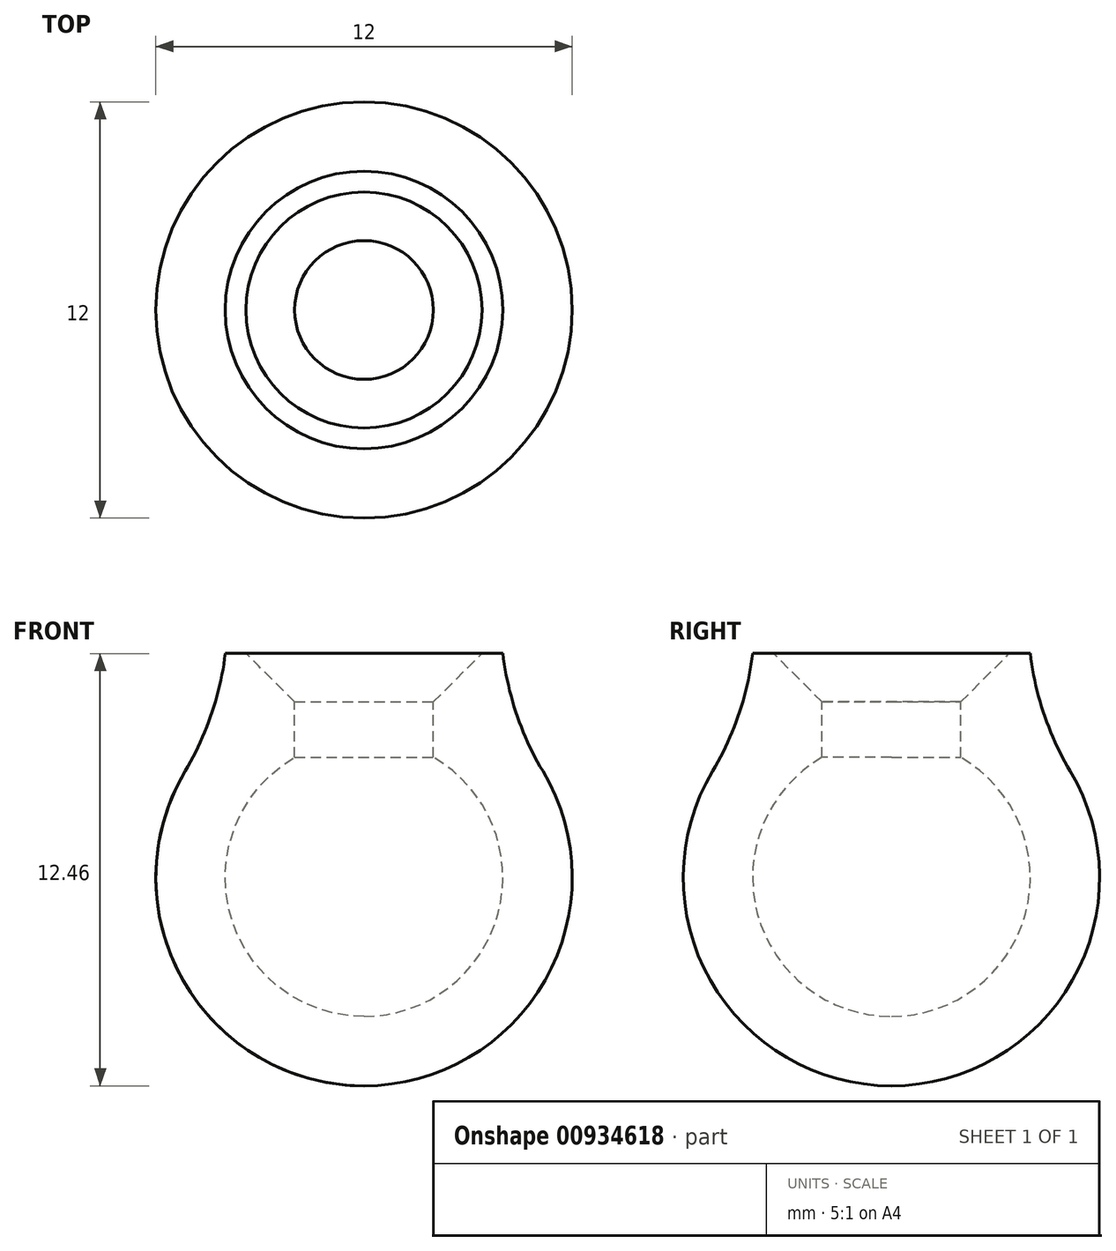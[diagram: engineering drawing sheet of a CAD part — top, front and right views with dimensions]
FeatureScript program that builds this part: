
annotation { "Feature Type Name" : "Feature", "Feature Type Description" : "" }
export const myFeature = defineFeature(function(context is Context, id is Id, definition is map)
    precondition{}
    {
        {
            var Q0;
            Q0=qCreatedBy(makeId("Front.planeOp"),FACE);
            var sketch = newSketch(context, id + "F0", { "sketchPlane" : qUnion([Q0])});
            skArc(sketch, "E0", {"start": v(-2, 7.46) * mm, "mid": v(-3.86, 2.96) * mm, "end": v(0, 0) * mm});
            skLineSegment(sketch, "E1", {"start": v(-2, 7.46) * mm, "end": v(-2, 10.46) * mm});
            skArc(sketch, "E2.0", {"start": v(-4, 8.47) * mm, "mid": v(-5.6, 1.86) * mm, "end": v(0, -2) * mm});
            skLineSegment(sketch, "E2.1", {"start": v(-4, 8.47) * mm, "end": v(-4, 10.46) * mm});
            skLineSegment(sketch, "E3", {"start": v(-4, 10.46) * mm, "end": v(-2, 10.46) * mm});
            skLineSegment(sketch, "E4", {"start": v(0, 0) * mm, "end": v(0, -2) * mm});
            skSolve(sketch);
        }
        {
            var Q0;
            Q0=makeQuery(id+"F0.imprint","IMPRINT",FACE,{"disambiguationData":[TD([[makeQuery(id+"F0.imprint","IMPRINT",EDGE,{"derivedFrom":sQuery(id+"F0.wireOp",EDGE,"E0")}),-1.0]])]});
            var Q1;
            Q1=sQuery(id+"F0.wireOp",EDGE,"E0");
            var Q2;
            Q2=sQuery(id+"F0.wireOp",EDGE,"E2.0");
            var Q3;
            Q3=sQuery(id+"F0.wireOp",EDGE,"E2.1");
            var Q4;
            Q4=sQuery(id+"F0.wireOp",EDGE,"E1");
            var Q5;
            Q5=sQuery(id+"F0.wireOp",EDGE,"E4");
            revolve(context, id + "F1", {"surfaceOperationType" : NewSurfaceOperationType.NEW, "entities" : qUnion([Q0]), "surfaceEntities" : qUnion([Q1, Q2, Q3, Q4]), "axis" : qUnion([Q5]), "revolveType" : RevolveType.FULL});
        }
        {
            var Q0;
            Q0=makeQuery(id+"F1.opRevolve","SWEPT_EDGE",EDGE,{"disambiguationData":[OSD([sQuery(id+"F0.wireOp",EDGE,"E1"),sQuery(id+"F0.wireOp",EDGE,"E3")])]});
            chamfer(context, id + "F2", {"entities" : qUnion([Q0]), "width" : 1.4 * mm, "tangentPropagation" : true});
        }
        {
            var Q0;
            Q0=makeQuery(id+"F1.opRevolve","SWEPT_EDGE",EDGE,{"disambiguationData":[OSD([sQuery(id+"F0.wireOp",EDGE,"E2.0"),sQuery(id+"F0.wireOp",EDGE,"E2.1")])]});
            fillet(context, id + "F3", {"entities" : qUnion([Q0]), "radius" : 8.6 * mm, "tangentPropagation" : true, "allowEdgeOverflow" : false});
        }
    });
